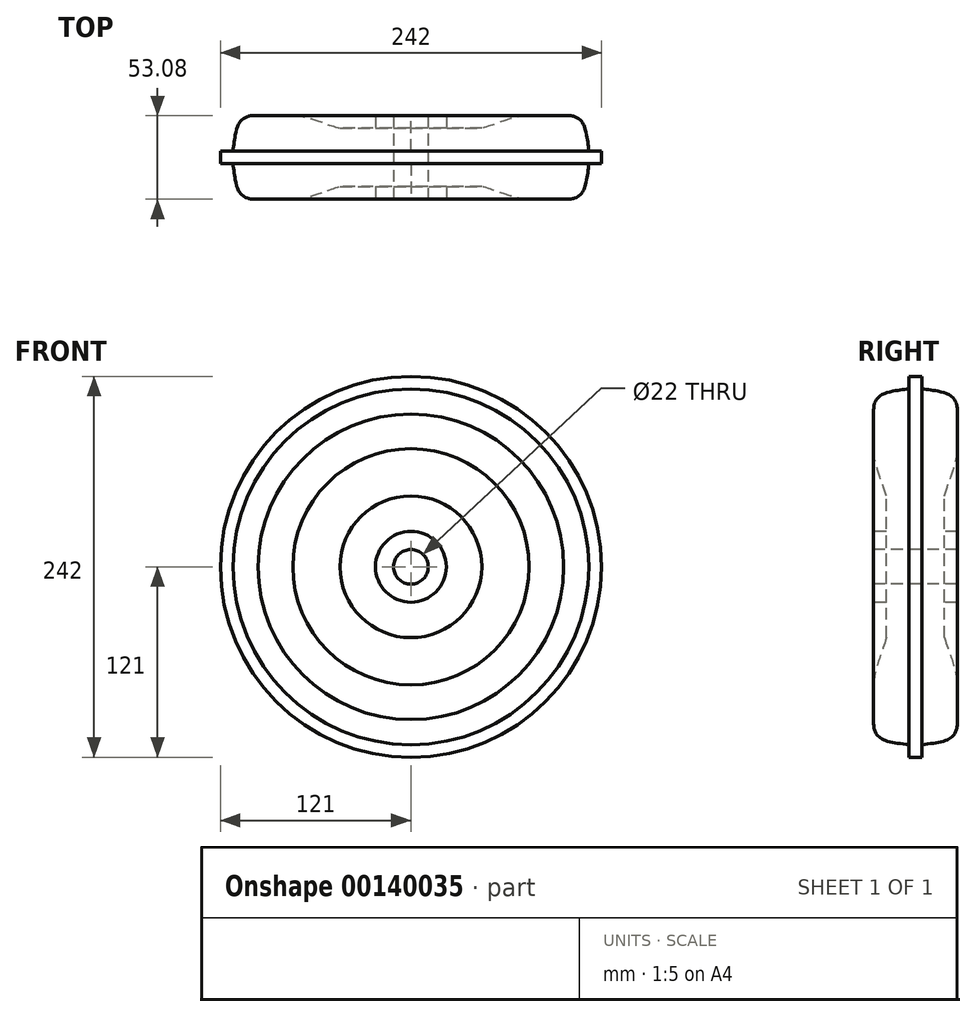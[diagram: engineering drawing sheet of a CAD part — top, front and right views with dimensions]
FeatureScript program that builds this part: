
annotation { "Feature Type Name" : "Feature", "Feature Type Description" : "" }
export const myFeature = defineFeature(function(context is Context, id is Id, definition is map)
    precondition{}
    {
        {
            var Q0;
            Q0=qCreatedBy(makeId("Right.planeOp"),FACE);
            var sketch = newSketch(context, id + "F0", { "sketchPlane" : qUnion([Q0])});
            skLineSegment(sketch, "E0", {"start": v(0, 0) * mm, "end": v(26.5, 0) * mm});
            skLineSegment(sketch, "E1", {"start": v(26.5, 0) * mm, "end": v(26.5, 22.5) * mm});
            skLineSegment(sketch, "E2", {"start": v(26.5, 22.5) * mm, "end": v(18.5, 22.5) * mm});
            skLineSegment(sketch, "E3", {"start": v(18.5, 22.5) * mm, "end": v(18.5, 45) * mm});
            skLineSegment(sketch, "E4", {"start": v(4, 113) * mm, "end": v(4, 121) * mm});
            skLineSegment(sketch, "E5", {"start": v(4, 121) * mm, "end": v(0, 121) * mm});
            skLineSegment(sketch, "E6", {"start": v(0, 121) * mm, "end": v(0, 0) * mm, "construction": true});
            skFitSpline(sketch, "E7", {"points": [v(4, 113) * mm, v(18.36, 110.57) * mm, v(23.9, 107.32) * mm, v(26.08, 103.45) * mm, v(26.5, 97.03) * mm], "startDerivative": vector(46.4, -5.1) * mm, "endDerivative": vector(-1.25, -50.08) * mm});
            skFitSpline(sketch, "E8", {"points": [v(18.5, 45) * mm, v(22.15, 56.1) * mm, v(24.5, 63.27) * mm, v(25.95, 68.85) * mm, v(26.5, 75.03) * mm], "startDerivative": vector(10, 37.98) * mm, "endDerivative": vector(0.53, 32.2) * mm});
            skLineSegment(sketch, "E9", {"start": v(26.5, 97.03) * mm, "end": v(26.5, 75.03) * mm});
            skLineSegment(sketch, "E10.MirrorCS", {"start": v(-4, 121) * mm, "end": v(0, 121) * mm});
            skFitSpline(sketch, "E11.MirrorCS", {"points": [v(-4, 113) * mm, v(-18.36, 110.57) * mm, v(-23.9, 107.32) * mm, v(-26.08, 103.45) * mm, v(-26.5, 97.03) * mm], "startDerivative": vector(-46.4, -5.1) * mm, "endDerivative": vector(1.25, -50.08) * mm});
            skLineSegment(sketch, "E12.MirrorCS", {"start": v(-26.5, 97.03) * mm, "end": v(-26.5, 75.03) * mm});
            skLineSegment(sketch, "E13.MirrorCS", {"start": v(-26.5, 0) * mm, "end": v(-26.5, 22.5) * mm});
            skLineSegment(sketch, "E14.MirrorCS", {"start": v(0, 0) * mm, "end": v(-26.5, 0) * mm});
            skLineSegment(sketch, "E15.MirrorCS", {"start": v(-18.5, 22.5) * mm, "end": v(-18.5, 45) * mm});
            skLineSegment(sketch, "E16.MirrorCS", {"start": v(-26.5, 22.5) * mm, "end": v(-18.5, 22.5) * mm});
            skLineSegment(sketch, "E17.MirrorCS", {"start": v(-4, 113) * mm, "end": v(-4, 121) * mm});
            skFitSpline(sketch, "E18.MirrorCS", {"points": [v(-18.5, 45) * mm, v(-22.15, 56.1) * mm, v(-24.5, 63.27) * mm, v(-25.95, 68.85) * mm, v(-26.5, 75.03) * mm], "startDerivative": vector(-10, 37.98) * mm, "endDerivative": vector(-0.53, 32.2) * mm});
            skSolve(sketch);
        }
        {
            var Q0;
            Q0 = qSketchRegion(id + "F0", true);
            var Q1;
            Q1=sQuery(id+"F0.wireOp",EDGE,"E0");
            revolve(context, id + "F1", {"entities" : qUnion([Q0]), "axis" : qUnion([Q1]), "revolveType" : RevolveType.FULL});
        }
        {
            var Q0;
            Q0=makeQuery(id+"F1.opRevolve","SWEPT_FACE",FACE,{"disambiguationData":[OSD([sQuery(id+"F0.wireOp",EDGE,"E13.MirrorCS")])]});
            var sketch = newSketch(context, id + "F2", { "sketchPlane" : qUnion([Q0])});
            skCircle(sketch, "E19", {"center": v(0, 0) * mm, "radius": 11 * mm});
            skSolve(sketch);
        }
        {
            var Q0;
            Q0=makeQuery(id+"F2.imprint","IMPRINT",FACE,{"disambiguationData":[TD([[makeQuery(id+"F2.imprint","IMPRINT",EDGE,{"derivedFrom":sQuery(id+"F2.wireOp",EDGE,"E19")}),1.0]])]});
            var Q1;
            Q1=sQuery(id+"F2.wireOp",EDGE,"E19");
            extrude(context, id + "F3", {"entities" : qUnion([Q0]), "operationType" : NewBodyOperationType.REMOVE, "surfaceEntities" : qUnion([Q1]), "endBound" : BoundingType.THROUGH_ALL, "oppositeDirection" : true, "depth" : 25 * mm});
        }
    });
